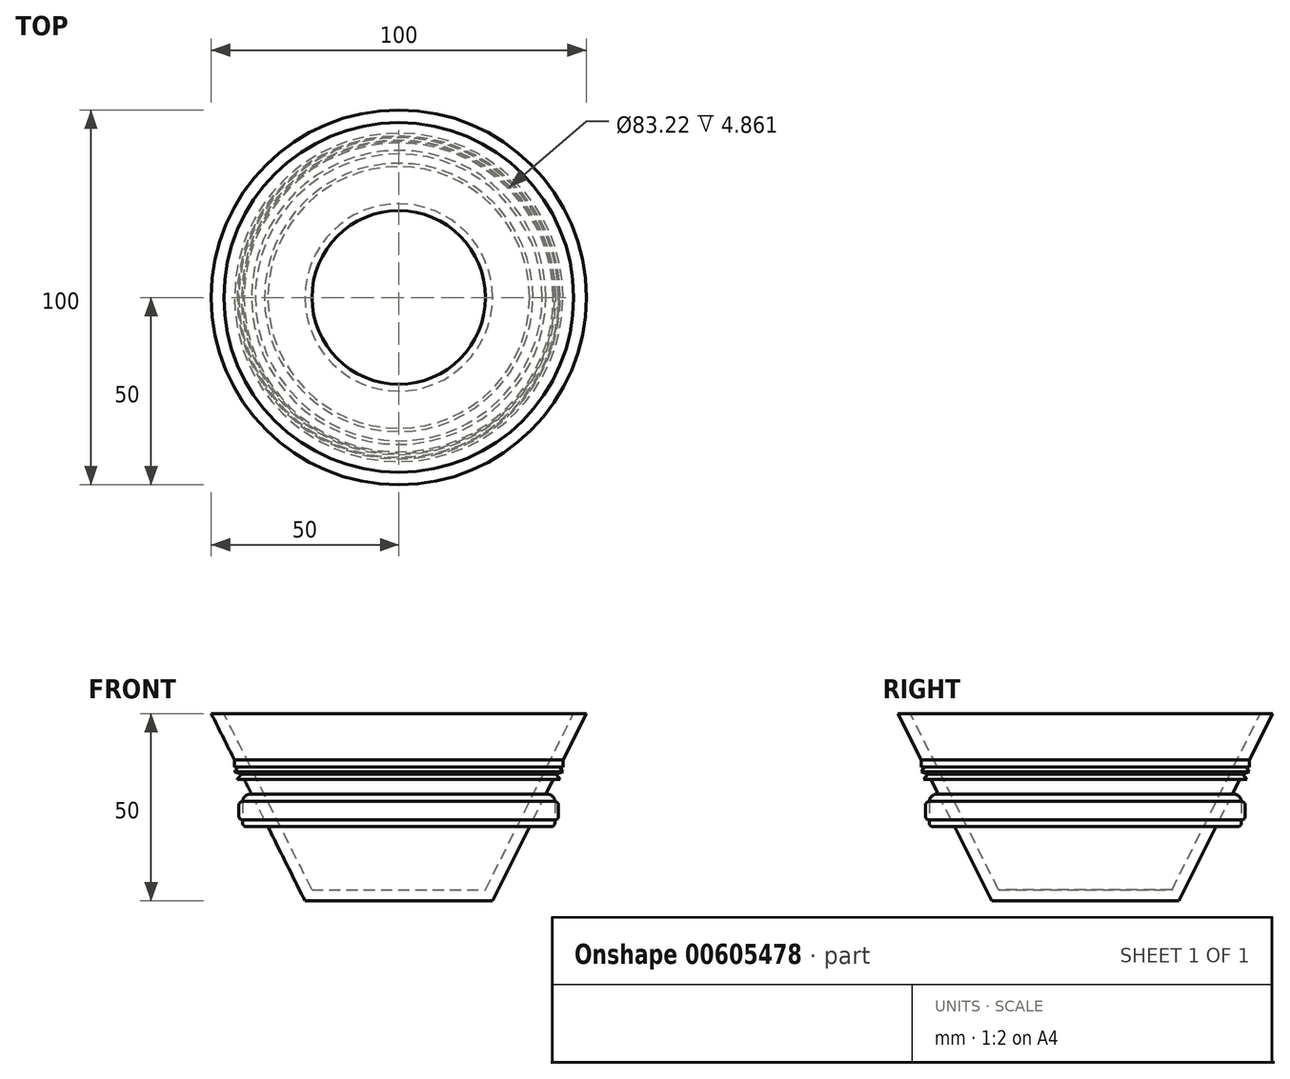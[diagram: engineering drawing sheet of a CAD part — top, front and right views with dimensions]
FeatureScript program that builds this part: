
annotation { "Feature Type Name" : "Feature", "Feature Type Description" : "" }
export const myFeature = defineFeature(function(context is Context, id is Id, definition is map)
    precondition{}
    {
        {
            var Q0;
            Q0=qCreatedBy(makeId("Front.planeOp"),FACE);
            var sketch = newSketch(context, id + "F0", { "sketchPlane" : qUnion([Q0])});
            skLineSegment(sketch, "E0", {"start": v(0, 0) * mm, "end": v(0, 50) * mm, "construction": true});
            skLineSegment(sketch, "E1", {"start": v(0, 0) * mm, "end": v(25, 0) * mm});
            skLineSegment(sketch, "E2", {"start": v(25, 0) * mm, "end": v(50, 50) * mm});
            skLineSegment(sketch, "E3.0", {"start": v(23.15, 3) * mm, "end": v(46.65, 50) * mm});
            skLineSegment(sketch, "E3.1", {"start": v(0, 3) * mm, "end": v(23.15, 3) * mm});
            skLineSegment(sketch, "E4", {"start": v(0, 3) * mm, "end": v(0, 0) * mm});
            skLineSegment(sketch, "E5", {"start": v(46.65, 50) * mm, "end": v(50, 50) * mm});
            skLineSegment(sketch, "E6", {"start": v(43.8, 37.58) * mm, "end": v(43.8, 35.66) * mm});
            skLineSegment(sketch, "E7", {"start": v(43.8, 35.66) * mm, "end": v(42.83, 35.66) * mm});
            skLineSegment(sketch, "E8", {"start": v(42.83, 35.66) * mm, "end": v(43.8, 34.42) * mm});
            skLineSegment(sketch, "E9", {"start": v(43.8, 34.42) * mm, "end": v(41.94, 33.87) * mm});
            skLineSegment(sketch, "E10", {"start": v(41.94, 33.87) * mm, "end": v(43.08, 32.42) * mm});
            skLineSegment(sketch, "E11", {"start": v(43.08, 32.42) * mm, "end": v(41.2, 32.42) * mm});
            skLineSegment(sketch, "E12", {"start": v(39.23, 28.46) * mm, "end": v(39.61, 28.46) * mm});
            skLineSegment(sketch, "E13", {"start": v(41.61, 26.46) * mm, "end": v(41.61, 20.76) * mm});
            skLineSegment(sketch, "E14", {"start": v(40.65, 19.8) * mm, "end": v(34.9, 19.8) * mm});
            skLineSegment(sketch, "E15", {"start": v(34.9, 19.8) * mm, "end": v(35.8, 21.6) * mm});
            skLineSegment(sketch, "E16", {"start": v(35.8, 21.6) * mm, "end": v(41.62, 21.6) * mm});
            skLineSegment(sketch, "E17", {"start": v(42.62, 22.6) * mm, "end": v(42.62, 25.53) * mm});
            skLineSegment(sketch, "E18", {"start": v(41.62, 26.53) * mm, "end": v(38.27, 26.53) * mm});
            skLineSegment(sketch, "E19", {"start": v(38.27, 26.53) * mm, "end": v(35.8, 21.6) * mm});
            skPoint(sketch, "E20.visualSharp", {"position": v(41.61, 28.46) * mm});
            skArc(sketch, "E20.filletArc", {"start": v(41.61, 26.46) * mm, "mid": v(41.03, 27.87) * mm, "end": v(39.61, 28.46) * mm});
            skPoint(sketch, "E21.visualSharp", {"position": v(41.61, 19.8) * mm});
            skArc(sketch, "E21.filletArc", {"start": v(40.65, 19.8) * mm, "mid": v(41.33, 20.08) * mm, "end": v(41.61, 20.76) * mm});
            skPoint(sketch, "E22.visualSharp", {"position": v(42.62, 26.53) * mm});
            skArc(sketch, "E22.filletArc", {"start": v(42.62, 25.53) * mm, "mid": v(42.32, 26.24) * mm, "end": v(41.62, 26.53) * mm});
            skPoint(sketch, "E23.visualSharp", {"position": v(42.62, 21.6) * mm});
            skArc(sketch, "E23.filletArc", {"start": v(41.62, 21.6) * mm, "mid": v(42.32, 21.9) * mm, "end": v(42.62, 22.6) * mm});
            skSolve(sketch);
        }
        {
            var Q0;
            Q0=makeQuery(id+"F0.imprint","IMPRINT",FACE,{"disambiguationData":[TD([[makeQuery(id+"F0.imprint","IMPRINT",EDGE,{"derivedFrom":sQuery(id+"F0.wireOp",EDGE,"E1")}),1.0]])]});
            var Q1;
            {var subQ0=sQuery(id+"F0.wireOp",EDGE,"E6");Q1=makeQuery(id+"F0.imprint","IMPRINT",FACE,{"disambiguationData":[TD([[makeQuery(id+"F0.imprint","IMPRINT",EDGE,{"derivedFrom":subQ0}),-1.0]])]});}
            var Q2;
            {var subQ0=sQuery(id+"F0.wireOp",EDGE,"E8");Q2=makeQuery(id+"F0.imprint","IMPRINT",FACE,{"disambiguationData":[TD([[makeQuery(id+"F0.imprint","IMPRINT",EDGE,{"derivedFrom":subQ0}),-1.0]])]});}
            var Q3;
            {var subQ0=sQuery(id+"F0.wireOp",EDGE,"E10");Q3=makeQuery(id+"F0.imprint","IMPRINT",FACE,{"disambiguationData":[TD([[makeQuery(id+"F0.imprint","IMPRINT",EDGE,{"derivedFrom":subQ0}),-1.0]])]});}
            var Q4;
            Q4=makeQuery(id+"F0.imprint","IMPRINT",FACE,{"disambiguationData":[TD([[makeQuery(id+"F0.imprint","IMPRINT",EDGE,{"derivedFrom":sQuery(id+"F0.wireOp",EDGE,"E17")}),1.0]])]});
            var Q5;
            Q5=makeQuery(id+"F0.imprint","IMPRINT",FACE,{"disambiguationData":[TD([[makeQuery(id+"F0.imprint","IMPRINT",EDGE,{"derivedFrom":sQuery(id+"F0.wireOp",EDGE,"E14")}),-1.0]])]});
            var Q6;
            {var subQ0=sQuery(id+"F0.wireOp",EDGE,"E12");Q6=makeQuery(id+"F0.imprint","IMPRINT",FACE,{"disambiguationData":[TD([[makeQuery(id+"F0.imprint","IMPRINT",EDGE,{"derivedFrom":subQ0}),-1.0]])]});}
            var Q7;
            Q7=sQuery(id+"F0.wireOp",EDGE,"E0");
            revolve(context, id + "F1", {"entities" : qUnion([Q0, Q1, Q2, Q3, Q4, Q5, Q6]), "axis" : qUnion([Q7]), "revolveType" : RevolveType.FULL});
        }
    });
